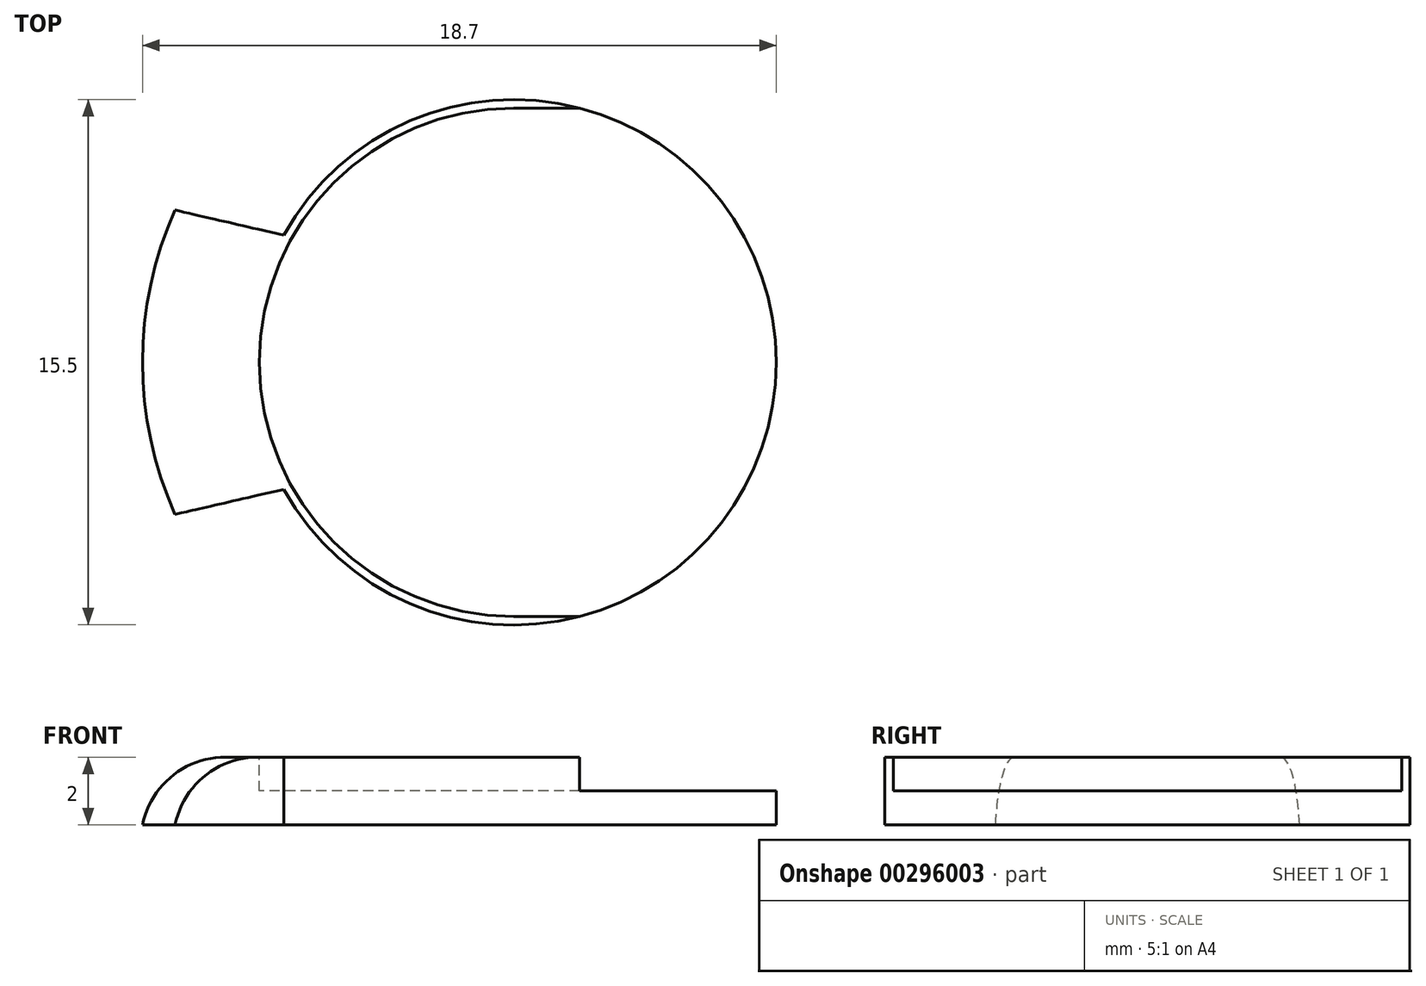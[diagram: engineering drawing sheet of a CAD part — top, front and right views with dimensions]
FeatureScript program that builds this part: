
annotation { "Feature Type Name" : "Feature", "Feature Type Description" : "" }
export const myFeature = defineFeature(function(context is Context, id is Id, definition is map)
    precondition{}
    {
        {
            var Q0;
            Q0=qCreatedBy(makeId("Top.planeOp"),FACE);
            var sketch = newSketch(context, id + "F0", { "sketchPlane" : qUnion([Q0])});
            skCircle(sketch, "E0", {"center": v(0, 0) * mm, "radius": 7.75 * mm});
            skLineSegment(sketch, "E1", {"start": v(-6.78, 3.75) * mm, "end": v(-6.78, -3.75) * mm});
            skLineSegment(sketch, "E2", {"start": v(0, 0) * mm, "end": v(30, 0) * mm, "construction": true});
            skArc(sketch, "E3.0.startCap", {"start": v(0, -11) * mm, "mid": v(-11, 0) * mm, "end": v(0, 11) * mm});
            skArc(sketch, "E3.0.endCap", {"start": v(30, 11) * mm, "mid": v(41, 0) * mm, "end": v(30, -11) * mm});
            skLineSegment(sketch, "E3.0.left", {"start": v(0, 11) * mm, "end": v(30, 11) * mm});
            skLineSegment(sketch, "E3.0.right", {"start": v(0, -11) * mm, "end": v(30, -11) * mm});
            skLineSegment(sketch, "E4", {"start": v(-6.78, 3.75) * mm, "end": v(-10.04, 4.5) * mm});
            skLineSegment(sketch, "E5", {"start": v(-10.04, 4.5) * mm, "end": v(-10.04, -4.5) * mm});
            skLineSegment(sketch, "E6", {"start": v(-10.04, -4.5) * mm, "end": v(-6.78, -3.75) * mm});
            skCircle(sketch, "E7", {"center": v(35, 0) * mm, "radius": 2.5 * mm});
            skSolve(sketch);
        }
        {
            var Q0;
            {var subQ0=sQuery(id+"F0.wireOp",EDGE,"E5");Q0=makeQuery(id+"F0.imprint","IMPRINT",FACE,{"disambiguationData":[TD([[makeQuery(id+"F0.imprint","IMPRINT",EDGE,{"derivedFrom":subQ0}),-1.0]])]});}
            var Q1;
            {var subQ0=sQuery(id+"F0.wireOp",EDGE,"E4");Q1=makeQuery(id+"F0.imprint","IMPRINT",FACE,{"disambiguationData":[TD([[makeQuery(id+"F0.imprint","IMPRINT",EDGE,{"derivedFrom":subQ0}),1.0]])]});}
            var Q2;
            Q2=makeQuery(id+"F0.imprint","IMPRINT",FACE,{"disambiguationData":[TD([[makeQuery(id+"F0.imprint","IMPRINT",EDGE,{"derivedFrom":sQuery(id+"F0.wireOp",EDGE,"E3.0.endCap")}),-1.0]])]});
            var Q3;
            {var subQ0=sQuery(id+"F0.wireOp",EDGE,"E1");Q3=makeQuery(id+"F0.imprint","IMPRINT",FACE,{"disambiguationData":[TD([[makeQuery(id+"F0.imprint","IMPRINT",EDGE,{"derivedFrom":subQ0}),-1.0]])]});}
            var Q4;
            {var subQ0=sQuery(id+"F0.wireOp",EDGE,"E1");Q4=makeQuery(id+"F0.imprint","IMPRINT",FACE,{"disambiguationData":[TD([[makeQuery(id+"F0.imprint","IMPRINT",EDGE,{"derivedFrom":subQ0}),1.0]])]});}
            extrude(context, id + "F1", {"entities" : qUnion([Q0, Q1, Q2, Q3, Q4]), "depth" : 3 * mm});
        }
        {
            var Q0;
            Q0=makeQuery(id+"F1.opExtrude","CAP_EDGE",EDGE,{"disambiguationData":[OSD([sQuery(id+"F0.wireOp",EDGE,"E3.0.startCap")])],"isStart":false});
            fillet(context, id + "F2", {"entities" : qUnion([Q0]), "radius" : 2.5 * mm, "tangentPropagation" : true, "allowEdgeOverflow" : false});
        }
        {
            var Q0;
            {var subQ0=sQuery(id+"F0.wireOp",EDGE,"E5");Q0=makeQuery(id+"F0.imprint","IMPRINT",FACE,{"disambiguationData":[TD([[makeQuery(id+"F0.imprint","IMPRINT",EDGE,{"derivedFrom":subQ0}),-1.0]])]});}
            var Q1;
            {var subQ0=sQuery(id+"F0.wireOp",EDGE,"E4");Q1=makeQuery(id+"F0.imprint","IMPRINT",FACE,{"disambiguationData":[TD([[makeQuery(id+"F0.imprint","IMPRINT",EDGE,{"derivedFrom":subQ0}),1.0]])]});}
            var Q2;
            {var subQ0=sQuery(id+"F0.wireOp",EDGE,"E1");Q2=makeQuery(id+"F0.imprint","IMPRINT",FACE,{"disambiguationData":[TD([[makeQuery(id+"F0.imprint","IMPRINT",EDGE,{"derivedFrom":subQ0}),-1.0]])]});}
            var Q3;
            {var subQ0=sQuery(id+"F0.wireOp",EDGE,"E1");Q3=makeQuery(id+"F0.imprint","IMPRINT",FACE,{"disambiguationData":[TD([[makeQuery(id+"F0.imprint","IMPRINT",EDGE,{"derivedFrom":subQ0}),1.0]])]});}
            extrude(context, id + "F3", {"entities" : qUnion([Q0, Q1, Q2, Q3]), "operationType" : NewBodyOperationType.REMOVE, "depth" : 1 * mm});
        }
        {
            var Q0;
            Q0=makeQuery(id+"F1.opExtrude","CAP_FACE",FACE,{"disambiguationData":[OSD([sQuery(id+"F0.wireOp",EDGE,"E3.0.startCap"),sQuery(id+"F0.wireOp",EDGE,"E3.0.endCap"),sQuery(id+"F0.wireOp",EDGE,"E3.0.left"),sQuery(id+"F0.wireOp",EDGE,"E3.0.right"),sQuery(id+"F0.wireOp",EDGE,"E7")])],"isStart":false});
            var sketch = newSketch(context, id + "F4", { "sketchPlane" : qUnion([Q0])});
            skLineSegment(sketch, "E8.0", {"start": v(30, 8.5) * mm, "end": v(0, 8.5) * mm});
            skArc(sketch, "E8.1", {"start": v(0, 8.5) * mm, "mid": v(-8.5, 0) * mm, "end": v(0, -8.5) * mm});
            skLineSegment(sketch, "E8.2", {"start": v(0, -8.5) * mm, "end": v(30, -8.5) * mm});
            skArc(sketch, "E8.3", {"start": v(30, -8.5) * mm, "mid": v(38.5, 0) * mm, "end": v(30, 8.5) * mm});
            skCircle(sketch, "E8.4", {"center": v(35, 0) * mm, "radius": 2.5 * mm});
            skArc(sketch, "E9.0", {"start": v(0, 7.5) * mm, "mid": v(-7.5, 0) * mm, "end": v(0, -7.5) * mm});
            skLineSegment(sketch, "E9.1", {"start": v(30, 7.5) * mm, "end": v(0, 7.5) * mm});
            skArc(sketch, "E9.2", {"start": v(30, -7.5) * mm, "mid": v(37.5, 0) * mm, "end": v(30, 7.5) * mm});
            skLineSegment(sketch, "E9.3", {"start": v(0, -7.5) * mm, "end": v(30, -7.5) * mm});
            skCircle(sketch, "E10.0", {"center": v(35, 0) * mm, "radius": 3.5 * mm});
            skLineSegment(sketch, "E11.0", {"start": v(0, -13.5) * mm, "end": v(30, -13.5) * mm});
            skArc(sketch, "E11.1", {"start": v(0, 13.5) * mm, "mid": v(-13.5, 0) * mm, "end": v(0, -13.5) * mm});
            skLineSegment(sketch, "E11.2", {"start": v(30, 13.5) * mm, "end": v(0, 13.5) * mm});
            skArc(sketch, "E11.3", {"start": v(30, -13.5) * mm, "mid": v(43.5, 0) * mm, "end": v(30, 13.5) * mm});
            skSolve(sketch);
        }
        {
            var Q0;
            Q0=makeQuery(id+"F4.imprint","IMPRINT",FACE,{"disambiguationData":[TD([[makeQuery(id+"F4.imprint","IMPRINT",EDGE,{"derivedFrom":sQuery(id+"F4.wireOp",EDGE,"E9.0")}),1.0]])]});
            extrude(context, id + "F5", {"entities" : qUnion([Q0]), "operationType" : NewBodyOperationType.REMOVE, "oppositeDirection" : true, "depth" : 1 * mm});
        }
    });
